# Revit family: Slim_Line_Q15_ZUu_FOl
name_source: partatom
category: HLS-Bauteile
units: mm (PartAtom-declared; Revit-internal decimal feet)

## family parameters
Arbeitsebenenbasiert = Nein
Beim Laden mit Abzugskörper schneiden = Nein
Bemaßung runder Anschluss = Durchmesser verwenden
Gemeinsam genutzt = Nein
Immer vertikal = Ja
Klassifizierung = Keine
Raumberechnungspunkt = Nein
Teiletyp = Normal

## types (1)
- Slim_Line_Q15_ZUu_FOl
    B = 750 mm  [stored 2.46063 ft]
    Beschreibung = Gerät
    Classification.OmniClass.23.Description = Pre Fabricated Air Handling Units
    Classification.OmniClass.23.Number = 23-33 25 19
    Family.Subcategory.Abbreviation = AHU
    Family.Subcategory.Name = Air Handling Unit
    H = 2065 mm  [stored 6.77493 ft]
    Hersteller = Hansa
    L = 900 mm  [stored 2.95276 ft]
    Modell = Slim-Line-Q15
    RLT_Volumenstrom_max = 3250 m³/h
    Vorgabe-Ansicht = 0 mm  [stored 0 ft]

note: [stored X ft] marks values corroborated as IEEE doubles in the binary element streams (Revit-internal decimal feet)

## geometry (parser evidence)
native form markers: Sweep x1
no freeform markers — native parametric forms only
